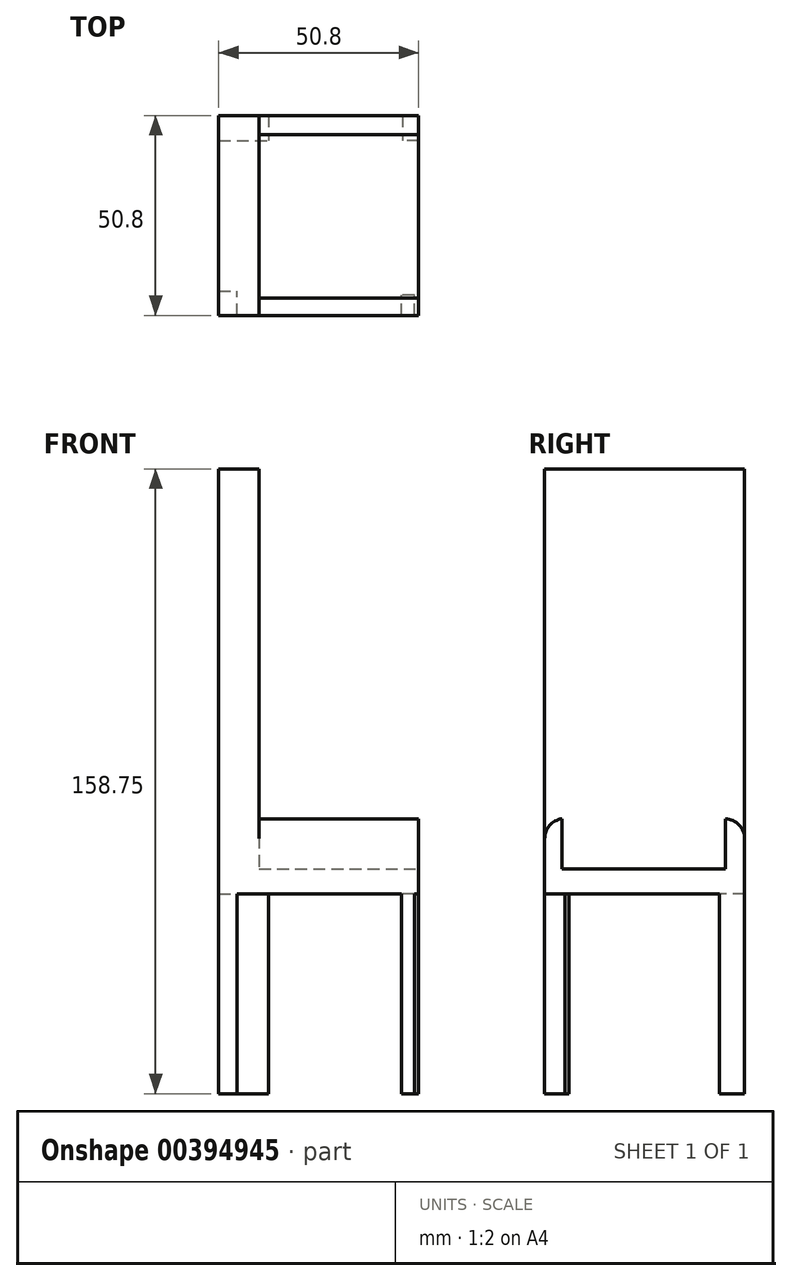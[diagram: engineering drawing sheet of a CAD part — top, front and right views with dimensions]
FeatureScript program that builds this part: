
annotation { "Feature Type Name" : "Feature", "Feature Type Description" : "" }
export const myFeature = defineFeature(function(context is Context, id is Id, definition is map)
    precondition{}
    {
        {
            var Q0;
            Q0=qCreatedBy(makeId("Top.planeOp"),FACE);
            var sketch = newSketch(context, id + "F0", { "sketchPlane" : qUnion([Q0])});
            skLineSegment(sketch, "E0.bottom", {"start": v(0, 0) * mm, "end": v(50.8, 0) * mm});
            skLineSegment(sketch, "E0.top", {"start": v(0, 50.8) * mm, "end": v(50.8, 50.8) * mm});
            skLineSegment(sketch, "E0.left", {"start": v(0, 0) * mm, "end": v(0, 50.8) * mm});
            skLineSegment(sketch, "E0.right", {"start": v(50.8, 0) * mm, "end": v(50.8, 50.8) * mm});
            skSolve(sketch);
        }
        {
            var Q0;
            Q0=makeQuery(id+"F0.imprint","IMPRINT",FACE,{"disambiguationData":[TD([[makeQuery(id+"F0.imprint","IMPRINT",EDGE,{"derivedFrom":sQuery(id+"F0.wireOp",EDGE,"E0.bottom")}),1.0]])]});
            extrude(context, id + "F1", {"entities" : qUnion([Q0]), "depth" : 6.35 * mm});
        }
        {
            var Q0;
            Q0=makeQuery(id+"F1.opExtrude","CAP_FACE",FACE,{"disambiguationData":[OSD([sQuery(id+"F0.wireOp",EDGE,"E0.bottom"),sQuery(id+"F0.wireOp",EDGE,"E0.top"),sQuery(id+"F0.wireOp",EDGE,"E0.left"),sQuery(id+"F0.wireOp",EDGE,"E0.right")])],"isStart":true});
            var sketch = newSketch(context, id + "F2", { "sketchPlane" : qUnion([Q0])});
            skLineSegment(sketch, "E1.bottom", {"start": v(49.68, 0) * mm, "end": v(46.39, 0) * mm});
            skLineSegment(sketch, "E1.top", {"start": v(49.68, -5.14) * mm, "end": v(46.39, -5.14) * mm});
            skLineSegment(sketch, "E1.left", {"start": v(49.68, 0) * mm, "end": v(49.68, -5.14) * mm});
            skLineSegment(sketch, "E1.right", {"start": v(46.39, 0) * mm, "end": v(46.39, -5.14) * mm});
            skLineSegment(sketch, "E2.bottom", {"start": v(0, 0) * mm, "end": v(4.67, 0) * mm});
            skLineSegment(sketch, "E2.top", {"start": v(0, -6.22) * mm, "end": v(4.67, -6.22) * mm});
            skLineSegment(sketch, "E2.left", {"start": v(0, 0) * mm, "end": v(0, -6.22) * mm});
            skLineSegment(sketch, "E2.right", {"start": v(4.67, 0) * mm, "end": v(4.67, -6.22) * mm});
            skLineSegment(sketch, "E3.bottom", {"start": v(50.8, -50.8) * mm, "end": v(46.7, -50.8) * mm});
            skLineSegment(sketch, "E3.top", {"start": v(50.8, -44.45) * mm, "end": v(46.7, -44.45) * mm});
            skLineSegment(sketch, "E3.left", {"start": v(50.8, -50.8) * mm, "end": v(50.8, -44.45) * mm});
            skLineSegment(sketch, "E3.right", {"start": v(46.7, -50.8) * mm, "end": v(46.7, -44.45) * mm});
            skLineSegment(sketch, "E4.bottom", {"start": v(0, -50.8) * mm, "end": v(12.7, -50.8) * mm});
            skLineSegment(sketch, "E4.top", {"start": v(0, -44.45) * mm, "end": v(12.7, -44.45) * mm});
            skLineSegment(sketch, "E4.left", {"start": v(0, -50.8) * mm, "end": v(0, -44.45) * mm});
            skLineSegment(sketch, "E4.right", {"start": v(12.7, -50.8) * mm, "end": v(12.7, -44.45) * mm});
            skLineSegment(sketch, "E5.bottom", {"start": v(49.68, 0) * mm, "end": v(49.68, 0) * mm});
            skLineSegment(sketch, "E5.top", {"start": v(49.68, -5.14) * mm, "end": v(49.68, -5.14) * mm});
            skSolve(sketch);
        }
        {
            var Q0;
            Q0 = qSketchRegion(id + "F2", true);
            extrude(context, id + "F3", {"entities" : qUnion([Q0]), "operationType" : NewBodyOperationType.ADD, "depth" : 25.4 * mm});
        }
        {
            var Q0;
            Q0=makeQuery(id+"F3.opExtrude","CAP_FACE",FACE,{"disambiguationData":[OSD([sQuery(id+"F2.wireOp",EDGE,"E1.bottom"),sQuery(id+"F2.wireOp",EDGE,"E1.top"),sQuery(id+"F2.wireOp",EDGE,"E1.right"),sQuery(id+"F2.wireOp",EDGE,"E1.left")])],"isStart":false});
            var Q1;
            Q1=makeQuery(id+"F3.opExtrude","CAP_FACE",FACE,{"disambiguationData":[OSD([sQuery(id+"F2.wireOp",EDGE,"E2.bottom"),sQuery(id+"F2.wireOp",EDGE,"E2.top"),sQuery(id+"F2.wireOp",EDGE,"E2.left"),sQuery(id+"F2.wireOp",EDGE,"E2.right")])],"isStart":false});
            var Q2;
            Q2=makeQuery(id+"F3.opExtrude","CAP_FACE",FACE,{"disambiguationData":[OSD([sQuery(id+"F2.wireOp",EDGE,"E4.bottom"),sQuery(id+"F2.wireOp",EDGE,"E4.top"),sQuery(id+"F2.wireOp",EDGE,"E4.left"),sQuery(id+"F2.wireOp",EDGE,"E4.right")])],"isStart":false});
            var Q3;
            Q3=makeQuery(id+"F3.opExtrude","CAP_FACE",FACE,{"disambiguationData":[OSD([sQuery(id+"F2.wireOp",EDGE,"E3.bottom"),sQuery(id+"F2.wireOp",EDGE,"E3.top"),sQuery(id+"F2.wireOp",EDGE,"E3.left"),sQuery(id+"F2.wireOp",EDGE,"E3.right")])],"isStart":false});
            extrude(context, id + "F4", {"entities" : qUnion([Q0, Q1, Q2, Q3]), "operationType" : NewBodyOperationType.ADD, "depth" : 25.4 * mm});
        }
        {
            var Q0;
            Q0=makeQuery(id+"F1.opExtrude","CAP_FACE",FACE,{"disambiguationData":[OSD([sQuery(id+"F0.wireOp",EDGE,"E0.bottom"),sQuery(id+"F0.wireOp",EDGE,"E0.top"),sQuery(id+"F0.wireOp",EDGE,"E0.left"),sQuery(id+"F0.wireOp",EDGE,"E0.right")])],"isStart":false});
            var sketch = newSketch(context, id + "F5", { "sketchPlane" : qUnion([Q0])});
            skLineSegment(sketch, "E6.bottom", {"start": v(0, 0) * mm, "end": v(10.24, 0) * mm});
            skLineSegment(sketch, "E6.top", {"start": v(0, 50.8) * mm, "end": v(10.24, 50.8) * mm});
            skLineSegment(sketch, "E6.left", {"start": v(0, 0) * mm, "end": v(0, 50.8) * mm});
            skLineSegment(sketch, "E6.right", {"start": v(10.24, 0) * mm, "end": v(10.24, 50.8) * mm});
            skSolve(sketch);
        }
        {
            var Q0;
            Q0 = qSketchRegion(id + "F5", true);
            extrude(context, id + "F6", {"entities" : qUnion([Q0]), "operationType" : NewBodyOperationType.ADD, "depth" : 101.6 * mm});
        }
        {
            var Q0;
            Q0=makeQuery(id+"F1.opExtrude","CAP_FACE",FACE,{"disambiguationData":[OSD([sQuery(id+"F0.wireOp",EDGE,"E0.bottom"),sQuery(id+"F0.wireOp",EDGE,"E0.top"),sQuery(id+"F0.wireOp",EDGE,"E0.left"),sQuery(id+"F0.wireOp",EDGE,"E0.right")])],"isStart":false});
            var sketch = newSketch(context, id + "F7", { "sketchPlane" : qUnion([Q0])});
            skLineSegment(sketch, "E7.bottom", {"start": v(10.24, 0) * mm, "end": v(50.8, 0) * mm});
            skLineSegment(sketch, "E7.top", {"start": v(10.24, 4.4) * mm, "end": v(50.8, 4.4) * mm});
            skLineSegment(sketch, "E7.left", {"start": v(10.24, 0) * mm, "end": v(10.24, 4.4) * mm});
            skLineSegment(sketch, "E7.right", {"start": v(50.8, 0) * mm, "end": v(50.8, 4.4) * mm});
            skSolve(sketch);
        }
        {
            var Q0;
            Q0 = qSketchRegion(id + "F7", true);
            extrude(context, id + "F8", {"entities" : qUnion([Q0]), "operationType" : NewBodyOperationType.ADD, "depth" : 12.7 * mm});
        }
        {
            var Q0;
            Q0=makeQuery(id+"F1.opExtrude","CAP_FACE",FACE,{"disambiguationData":[OSD([sQuery(id+"F0.wireOp",EDGE,"E0.bottom"),sQuery(id+"F0.wireOp",EDGE,"E0.top"),sQuery(id+"F0.wireOp",EDGE,"E0.left"),sQuery(id+"F0.wireOp",EDGE,"E0.right")])],"isStart":false});
            var sketch = newSketch(context, id + "F9", { "sketchPlane" : qUnion([Q0])});
            skLineSegment(sketch, "E8.bottom", {"start": v(10.24, 50.8) * mm, "end": v(50.8, 50.8) * mm});
            skLineSegment(sketch, "E8.top", {"start": v(10.24, 45.9) * mm, "end": v(50.8, 45.9) * mm});
            skLineSegment(sketch, "E8.left", {"start": v(10.24, 50.8) * mm, "end": v(10.24, 45.9) * mm});
            skLineSegment(sketch, "E8.right", {"start": v(50.8, 50.8) * mm, "end": v(50.8, 45.9) * mm});
            skSolve(sketch);
        }
        {
            var Q0;
            Q0=makeQuery(id+"F9.imprint","IMPRINT",FACE,{"disambiguationData":[TD([[makeQuery(id+"F9.imprint","IMPRINT",EDGE,{"derivedFrom":sQuery(id+"F9.wireOp",EDGE,"E8.bottom")}),-1.0]])]});
            extrude(context, id + "F10", {"entities" : qUnion([Q0]), "operationType" : NewBodyOperationType.ADD, "depth" : 12.7 * mm});
        }
        {
            var Q0;
            Q0=makeQuery(id+"F8.opExtrude","CAP_EDGE",EDGE,{"disambiguationData":[OSD([sQuery(id+"F7.wireOp",EDGE,"E7.bottom")])],"isStart":false});
            fillet(context, id + "F11", {"entities" : qUnion([Q0]), "radius" : 5.08 * mm, "tangentPropagation" : true, "allowEdgeOverflow" : false});
        }
        {
            var Q0;
            Q0=makeQuery(id+"F10.opExtrude","CAP_EDGE",EDGE,{"disambiguationData":[OSD([sQuery(id+"F9.wireOp",EDGE,"E8.bottom")])],"isStart":false});
            fillet(context, id + "F12", {"entities" : qUnion([Q0]), "radius" : 5.08 * mm, "tangentPropagation" : true, "allowEdgeOverflow" : false});
        }
    });
